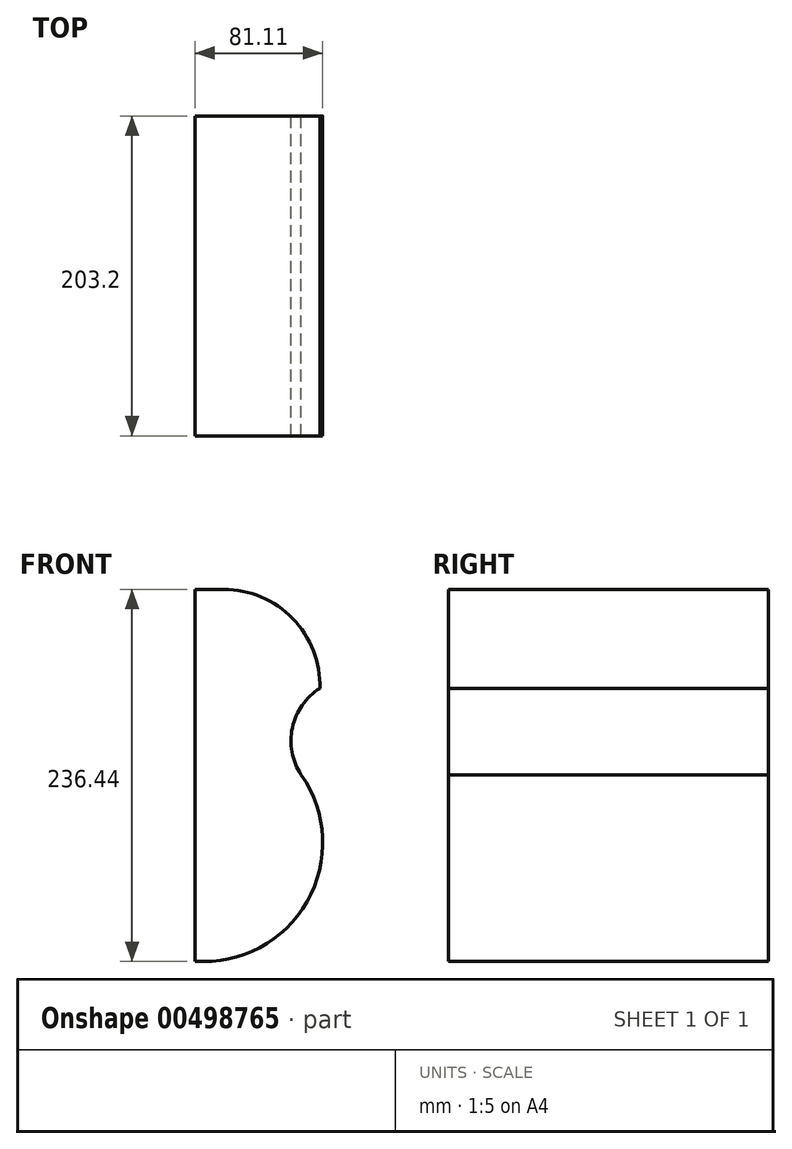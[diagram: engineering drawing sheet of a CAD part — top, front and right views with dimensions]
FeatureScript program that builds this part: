
annotation { "Feature Type Name" : "Feature", "Feature Type Description" : "" }
export const myFeature = defineFeature(function(context is Context, id is Id, definition is map)
    precondition{}
    {
        {
            var Q0;
            Q0=qCreatedBy(makeId("Front.planeOp"),FACE);
            var sketch = newSketch(context, id + "F0", { "sketchPlane" : qUnion([Q0])});
            skLineSegment(sketch, "E0", {"start": v(-78.6, 98.98) * mm, "end": v(-78.6, -137.24) * mm});
            skLineSegment(sketch, "E1", {"start": v(-78.6, 98.98) * mm, "end": v(-60.34, 98.98) * mm});
            skArc(sketch, "E2", {"start": v(0.74, 36.03) * mm, "mid": v(-16.49, 80.42) * mm, "end": v(-60.34, 98.98) * mm});
            skArc(sketch, "E3", {"start": v(0.74, 36.03) * mm, "mid": v(-16.75, 11.1) * mm, "end": v(-11.1, -18.82) * mm});
            skArc(sketch, "E4", {"start": v(-78.6, -137.24) * mm, "mid": v(-7.38, -99.39) * mm, "end": v(-11.1, -18.82) * mm});
            skSolve(sketch);
        }
        {
            var Q0;
            Q0=makeQuery(id+"F0.imprint","IMPRINT",FACE,{"disambiguationData":[TD([[makeQuery(id+"F0.imprint","IMPRINT",EDGE,{"derivedFrom":sQuery(id+"F0.wireOp",EDGE,"E0")}),1.0]])]});
            extrude(context, id + "F1", {"entities" : qUnion([Q0]), "depth" : 203.2 * mm});
        }
    });
